# Revit family: FU_Stool_Sandler_Woodlook 3-9
name_source: partatom
category: Furniture
units: mm (PartAtom-declared; Revit-internal decimal feet)

## family parameters
Always vertical = Yes
Cut with Voids When Loaded = No
OmniClass Number = 23.40.20.00
OmniClass Title = General Furniture and Specialties
Room Calculation Point = No
Shared = No
Work Plane-Based = No

## types (2) — shared parameters
Depth = 545 mm  [stored 1.78806 ft]
Height = 1080 mm  [stored 3.54331 ft]
Manufacturer = Sandler
URL = https://www.sandlerseating.com
Width = 480 mm  [stored 1.5748 ft]
zero-valued in all types: Default Elevation

## per-type parameters (varying)
| type | Description | Grab Handle | Upholstery | Woodlook |
| Woodlook 3.9 | Woodlook bar stool with frame manufactured entirely from aluminum but with realistic appearance of wood. Highly durable and scratch resistant. | No | Fabric - Gravity - Frozen CPC27 | Woodlook - 24A Walnut |
| Woodlook 3.9GH | Woodlook bar stool with frame manufactured entirely from aluminum but with realistic appearance of wood. Highly durable and scratch resistant. With grip handle. | Yes | Woodlook Vinyl - Slate | Woodlook - 88 Grey |

note: column(s) folded — value = type name in every type: Model

note: [stored X ft] marks values corroborated as IEEE doubles in the binary element streams (Revit-internal decimal feet)

## geometry (parser evidence)
native form markers: Sweep x8
no freeform markers — native parametric forms only
